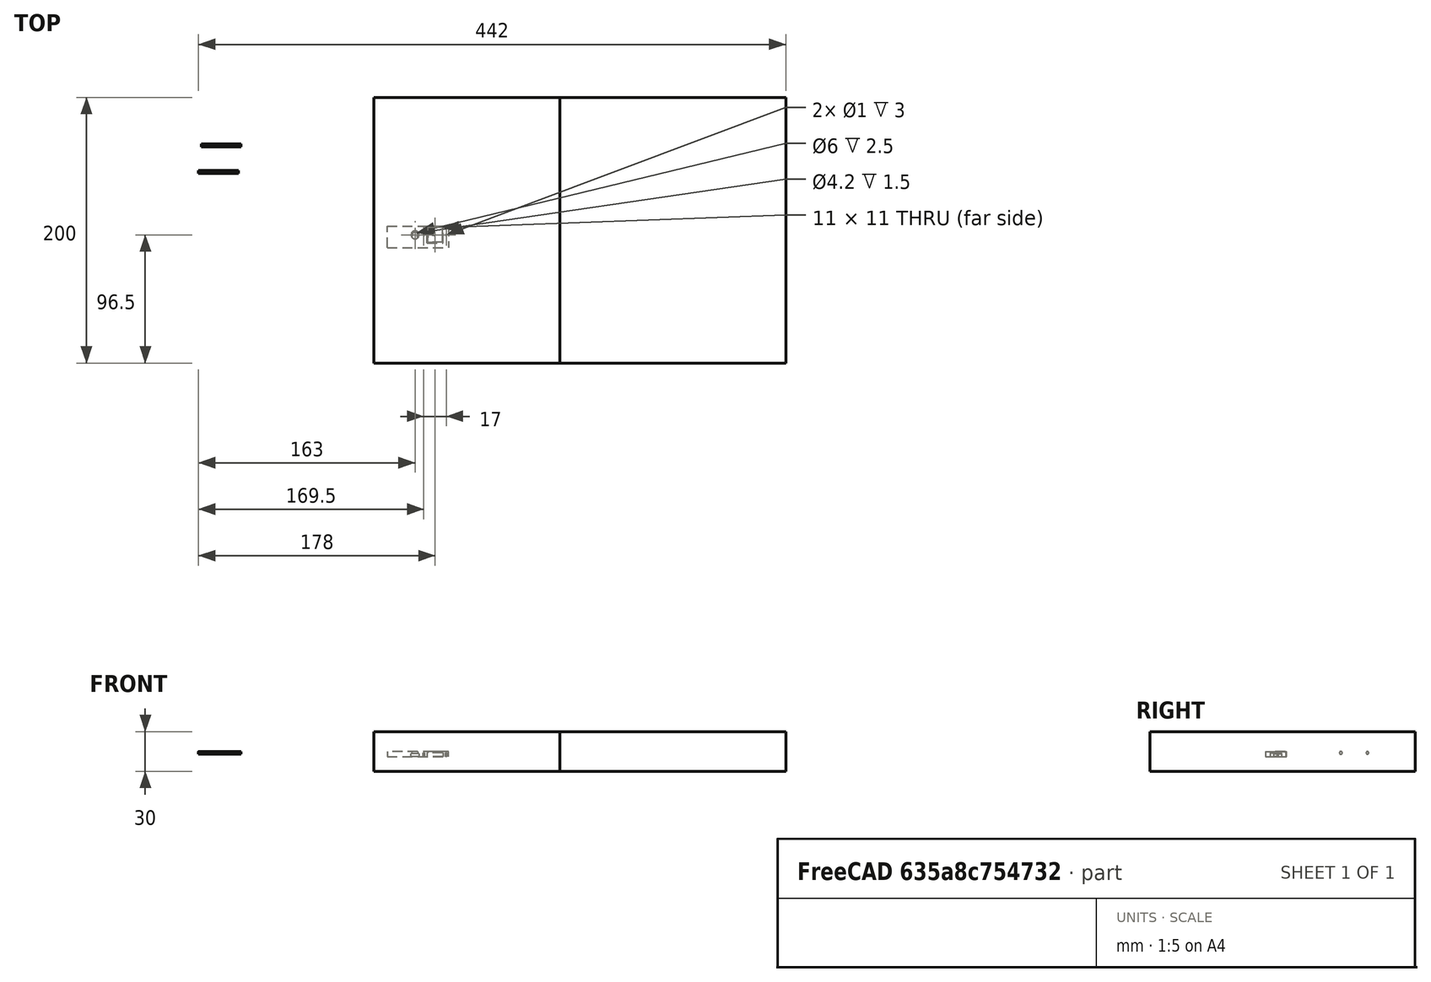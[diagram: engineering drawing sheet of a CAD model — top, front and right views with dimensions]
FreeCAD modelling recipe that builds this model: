
FCSTD DOCUMENT  (FreeCAD 0.17R13522 (Git))
Label: led_2
License: CreativeCommons Attribution-ShareAlike
LicenseURL: http://creativecommons.org/licenses/by-sa/4.0/
objects: Part::Cut×33, Part::Feature×29, Part::Box×10, Part::Fuse×7, Part::Part2DObjectPython×6, Part::Cylinder×4, App::DocumentObjectGroup×3
note: 89 computed .brp shape members not serialized (recipe doc carries the construction recipe); baked Part::Feature solids carry a one-line shape summary decoded from their .brp

FEATURE [Part::Part2DObjectPython] Line009  # Draft 2D object (typed FeaturePython)
  ChamferSize = 0
  Closed = false
  End = (270.847,20.2,0)
  FilletRadius = 0
  Length = 35.3471
  MakeFace = false
  Points = (2) [(235.5,20.2,0),(270.847,20.2,0)]
  Start = (235.5,20.2,0)
  Subdivisions = 0
FEATURE [Part::Part2DObjectPython] Circle001  # Draft 2D object (typed FeaturePython)
  FirstAngle = 0
  LastAngle = 0
  MakeFace = false
  Placement = pos=(259.67,20.2,0) rot=(0,0,1;0rad)
  Radius = 14
FEATURE [Part::Part2DObjectPython] Line014  # Draft 2D object (typed FeaturePython)
  ChamferSize = 0
  Closed = false
  End = (248.272,28.2144,0)
  FilletRadius = 0
  Length = 13.696
  MakeFace = false
  Placement = pos=(-10,0,-4) rot=(0,0,1;0rad)
  Points = (2) [(269.378,20.2,4),(258.272,28.2144,4)]
  Start = (259.378,20.2,0)
  Subdivisions = 0
FEATURE [Part::Part2DObjectPython] Line015  # Draft 2D object (typed FeaturePython)
  ChamferSize = 0
  Closed = false
  End = (254.876,33.263,0)
  FilletRadius = 0
  Length = 13.7518
  MakeFace = false
  Placement = pos=(-10,0,-4) rot=(0,0,1;0rad)
  Points = (2) [(269.174,20.2,4),(264.876,33.263,4)]
  Start = (259.174,20.2,0)
  Subdivisions = 0
FEATURE [Part::Part2DObjectPython] Line016  # Draft 2D object (typed FeaturePython)
  ChamferSize = 0
  Closed = false
  End = (263.227,33.6931,0)
  FilletRadius = 0
  Length = 14.1488
  MakeFace = false
  Placement = pos=(-10,0,-4) rot=(0,0,1;0rad)
  Points = (2) [(268.97,20.2,4),(273.227,33.6931,4)]
  Start = (258.97,20.2,0)
  Subdivisions = 0
FEATURE [Part::Part2DObjectPython] Line017  # Draft 2D object (typed FeaturePython)
  ChamferSize = 0
  Closed = false
  End = (270.612,28.9289,0)
  FilletRadius = 0
  Length = 14.5511
  MakeFace = false
  Placement = pos=(-10,0,-4) rot=(0,0,1;0rad)
  Points = (2) [(268.97,20.2,4),(280.612,28.9289,4)]
  Start = (258.97,20.2,0)
  Subdivisions = 0
FEATURE [App::DocumentObjectGroup] Construction
  Group = -> [Line009,Circle001,Line014,Line015,Line016,Line017]
FEATURE [Part::Box] Box001  label="Cube"
  AttacherType = Attacher::AttachEngine3D
  Height = 3
  Length = 6
  Placement = pos=(39,81,-108) rot=(0,0,1;0rad)
  Width = 6
FEATURE [Part::Feature] Fusion008001001061001  label="panel_siplays_encoders_dobles_y_spacers"
  Placement = pos=(0,0,-105) rot=(0,0,1;0rad)
  shape: bbox 280 x 210 x 10 mm, 411 faces (baked)
FEATURE [Part::Feature] Fusion003002001  label="el perforador001"
  Placement = pos=(48,115,-108) rot=(0,1,0;3.14159rad)
  shape: bbox 22 x 12 x 18 mm, 19 faces (baked)
FEATURE [Part::Feature] Fusion003002001001  label="el perforador002"
  Placement = pos=(87.5,115,-108) rot=(0,1,0;3.14159rad)
  shape: bbox 22 x 12 x 18 mm, 19 faces (baked)
FEATURE [Part::Cut] Cut001001001002003001008002002004
  Base = -> Fusion008001001061001
  Refine = true
  Tool = -> Fusion003002001
FEATURE [Part::Feature] Fusion003002001001001  label="el perforador003"
  Placement = pos=(127,115,-108) rot=(0,1,0;3.14159rad)
  shape: bbox 22 x 12 x 18 mm, 19 faces (baked)
FEATURE [Part::Cut] Cut001001001002003001008002002005
  Base = -> Cut001001001002003001008002002004
  Refine = true
  Tool = -> Fusion003002001001
FEATURE [Part::Feature] Fusion003002001001001001  label="el perforador004"
  Placement = pos=(166.5,115,-108) rot=(0,1,0;3.14159rad)
  shape: bbox 22 x 12 x 18 mm, 19 faces (baked)
FEATURE [Part::Feature] Fusion003002001001001001001  label="el perforador005"
  Placement = pos=(206,115,-108) rot=(0,1,0;3.14159rad)
  shape: bbox 22 x 12 x 18 mm, 19 faces (baked)
FEATURE [Part::Cut] Cut001001001002003001008002002006
  Base = -> Cut001001001002003001008002002005
  Refine = true
  Tool = -> Fusion003002001001001001
FEATURE [Part::Cut] Cut001001001002003001008002002007
  Base = -> Cut001001001002003001008002002006
  Refine = true
  Tool = -> Fusion003002001001001001001
FEATURE [Part::Feature] Fusion003002001001001001002001001  label="el perforador008"
  Placement = pos=(127,40,-108) rot=(0,1,0;3.14159rad)
  shape: bbox 22 x 12 x 18 mm, 19 faces (baked)
FEATURE [Part::Feature] Fusion003002001001001001002001002  label="el perforador009"
  Placement = pos=(127,80.5,-108) rot=(0,1,0;3.14159rad)
  shape: bbox 22 x 12 x 18 mm, 19 faces (baked)
FEATURE [Part::Feature] Fusion003002001001001001002001  label="el perforador007"
  Placement = pos=(127,55,-108) rot=(0,1,0;3.14159rad)
  shape: bbox 22 x 12 x 18 mm, 19 faces (baked)
FEATURE [Part::Feature] Fusion003002001001001001002  label="el perforador006"
  Placement = pos=(127,95.5,-108) rot=(0,1,0;3.14159rad)
  shape: bbox 22 x 12 x 18 mm, 19 faces (baked)
FEATURE [Part::Cut] Cut001001001002003001008002002008
  Base = -> Cut001001001002003001008002002007
  Refine = true
  Tool = -> Fusion003002001001001
FEATURE [Part::Cut] Cut001001001002003001008002002009
  Base = -> Cut001001001002003001008002002008
  Refine = true
  Tool = -> Fusion003002001001001001002
FEATURE [Part::Cut] Cut001001001002003001008002002010
  Base = -> Cut001001001002003001008002002009
  Refine = true
  Tool = -> Fusion003002001001001001002001
FEATURE [Part::Box] Box001001002002002001003001001004001001001001001001002  label="Cube034"
  AttacherType = Attacher::AttachEngine3D
  Height = 4
  Length = 32
  Placement = pos=(200,15,-108) rot=(0,0,1;0rad)
  Width = 10
FEATURE [Part::Fuse] Fusion003002001001001001002001003
  Base = -> Cut001001001002003001008002002010
  Refine = true
  Tool = -> Box001001002002002001003001001004001001001001001001002
FEATURE [Part::Fuse] Fusion003002001001001001002001004
  Base = -> Box001001002002002001003001001004001001001001001001002
  Refine = true
  Tool = -> Fusion003002001001001001002001003
FEATURE [Part::Fuse] Fusion003002001001001001002001005
  Refine = true
  Tool = -> Fusion003002001001001001002001004
FEATURE [Part::Fuse] Fusion003002001001001001002001006
  Base = -> Box001
  Refine = true
  Tool = -> Fusion003002001001001001002001005
FEATURE [Part::Feature] Fusion003002001001001001002001002001  label="el perforador010"
  Placement = pos=(47,80.5,-108) rot=(0,1,0;3.14159rad)
  shape: bbox 22 x 12 x 18 mm, 19 faces (baked)
FEATURE [Part::Feature] Fusion003002001001001001002001002002  label="el perforador011"
  Placement = pos=(87,80.5,-108) rot=(0,1,0;3.14159rad)
  shape: bbox 22 x 12 x 18 mm, 19 faces (baked)
FEATURE [Part::Feature] Fusion003002001001001001002001001001  label="el perforador012"
  Placement = pos=(87,40,-108) rot=(0,1,0;3.14159rad)
  shape: bbox 22 x 12 x 18 mm, 19 faces (baked)
FEATURE [Part::Feature] Fusion003002001001001001002001001001001  label="el perforador013"
  Placement = pos=(47,40,-108) rot=(0,1,0;3.14159rad)
  shape: bbox 22 x 12 x 18 mm, 19 faces (baked)
FEATURE [Part::Cut] Cut001001001002003001008002002011
  Base = -> Fusion003002001001001001002001006
  Refine = true
  Tool = -> Fusion003002001001001001002001002
FEATURE [Part::Cut] Cut001001001002003001008002002012
  Base = -> Cut001001001002003001008002002011
  Refine = true
  Tool = -> Fusion003002001001001001002001002002
FEATURE [Part::Cut] Cut001001001002003001008002002013
  Base = -> Cut001001001002003001008002002012
  Refine = true
  Tool = -> Fusion003002001001001001002001002001
FEATURE [Part::Cut] Cut001001001002003001008002002014
  Base = -> Cut001001001002003001008002002013
  Refine = true
  Tool = -> Fusion003002001001001001002001001001001
FEATURE [Part::Feature] Fusion003002001001001001002001001001002  label="el perforador014"
  Placement = pos=(220,8,-108) rot=(0.707107,0.707107,0;3.14159rad)
  shape: bbox 12 x 22 x 18 mm, 19 faces (baked)
FEATURE [Part::Cut] Cut001001001002003001008002002015
  Base = -> Cut001001001002003001008002002014
  Refine = true
  Tool = -> Fusion003002001001001001002001001001
FEATURE [Part::Cut] Cut001001001002003001008002002016
  Base = -> Cut001001001002003001008002002015
  Refine = true
  Tool = -> Fusion003002001001001001002001001
FEATURE [Part::Cut] Cut001001001002003001008002002017  label="base solo faltan los leds"
  Base = -> Cut001001001002003001008002002016
  Refine = true
  Tool = -> Fusion003002001001001001002001001001002
FEATURE [Part::Feature] Fusion001001  label="perforador led 3 mm001 rojo com2"
  Placement = pos=(24,43,-108) rot=(0,1,0;3.14159rad)
  shape: bbox 6 x 6 x 10 mm, 13 faces (baked)
FEATURE [Part::Feature] Fusion003002001001001001002001001001003  label="perforador led 3 mm002 rojo nav2"
  Placement = pos=(61,43,-108) rot=(0,1,0;3.14159rad)
  shape: bbox 6 x 6 x 10 mm, 13 faces (baked)
FEATURE [Part::Feature] Fusion003002001001001001002001001001004  label="perforador led 3 mm002 rojo adf2"
  Placement = pos=(101,43,-108) rot=(0,1,0;3.14159rad)
  shape: bbox 6 x 6 x 10 mm, 13 faces (baked)
FEATURE [Part::Feature] Fusion003002001001001001002001001001005  label="perforador led 3 mm001 rojo com1"
  Placement = pos=(24,83.5,-108) rot=(0,1,0;3.14159rad)
  shape: bbox 6 x 6 x 10 mm, 13 faces (baked)
FEATURE [Part::Feature] Fusion003002001001001001002001001001006  label="perforador led 3 mm002 rojo nav1"
  Placement = pos=(61,83.5,-108) rot=(0,1,0;3.14159rad)
  shape: bbox 6 x 6 x 10 mm, 13 faces (baked)
FEATURE [Part::Feature] Fusion003002001001001001002001001001007  label="perforador led 3 mm002 rojo adf1"
  Placement = pos=(101,83.5,-108) rot=(0,1,0;3.14159rad)
  shape: bbox 6 x 6 x 10 mm, 13 faces (baked)
FEATURE [Part::Cut] Cut
  Base = -> Cut001001001002003001008002002017
  Refine = true
  Tool = -> Fusion003002001001001001002001001001005
FEATURE [Part::Cut] Cut001001001002003001008002002018
  Base = -> Cut
  Refine = true
  Tool = -> Fusion003002001001001001002001001001006
FEATURE [Part::Cut] Cut001001001002003001008002002019
  Base = -> Cut001001001002003001008002002018
  Refine = true
  Tool = -> Fusion003002001001001001002001001001007
FEATURE [Part::Cut] Cut001001001002003001008002002020
  Base = -> Cut001001001002003001008002002019
  Refine = true
  Tool = -> Fusion003002001001001001002001001001004
FEATURE [Part::Cut] Cut001001001002003001008002002021
  Base = -> Cut001001001002003001008002002020
  Refine = true
  Tool = -> Fusion003002001001001001002001001001003
FEATURE [Part::Cut] Cut001001001002003001008002002022
  Base = -> Cut001001001002003001008002002021
  Refine = true
  Tool = -> Fusion001001
FEATURE [Part::Feature] Fusion003002001001001001002001001001008  label="perforador led 5 mm sound marker"
  Placement = pos=(40.75,133,-108) rot=(0,1,0;3.14159rad)
  shape: bbox 7.5 x 7.5 x 10 mm, 13 faces (baked)
FEATURE [Part::Feature] Fusion003002001001001001002001001001009  label="perforador led 5 mm sound com1"
  Placement = pos=(80.25,133,-108) rot=(0,1,0;3.14159rad)
  shape: bbox 7.5 x 7.5 x 10 mm, 13 faces (baked)
FEATURE [Part::Feature] Fusion003002001001001001002001001001010  label="perforador led 5 mm sound nav1"
  Placement = pos=(119.75,133,-108) rot=(0,1,0;3.14159rad)
  shape: bbox 7.5 x 7.5 x 10 mm, 13 faces (baked)
FEATURE [Part::Feature] Fusion003002001001001001002001001001011  label="perforador led 5 mm sound dme"
  Placement = pos=(159.25,133,-108) rot=(0,1,0;3.14159rad)
  shape: bbox 7.5 x 7.5 x 10 mm, 13 faces (baked)
FEATURE [Part::Feature] Fusion003002001001001001002001001001012  label="perforador led 5 mm sound adf1"
  Placement = pos=(198.75,133,-108) rot=(0,1,0;3.14159rad)
  shape: bbox 7.5 x 7.5 x 10 mm, 13 faces (baked)
FEATURE [Part::Feature] Fusion003002001001001001002001001001013  label="perforador led 5 mm ON/OFF"
  Placement = pos=(263.5,133,-108) rot=(0,1,0;3.14159rad)
  shape: bbox 7.5 x 7.5 x 10 mm, 13 faces (baked)
FEATURE [Part::Cut] Cut001001001002003001008002002023
  Base = -> Cut001001001002003001008002002022
  Refine = true
  Tool = -> Fusion003002001001001001002001001001013
FEATURE [Part::Cut] Cut001001001002003001008002002024
  Base = -> Cut001001001002003001008002002023
  Refine = true
  Tool = -> Fusion003002001001001001002001001001012
FEATURE [Part::Cut] Cut001001001002003001008002002025
  Base = -> Cut001001001002003001008002002024
  Refine = true
  Tool = -> Fusion003002001001001001002001001001011
FEATURE [Part::Cut] Cut001001001002003001008002002026
  Base = -> Cut001001001002003001008002002025
  Refine = true
  Tool = -> Fusion003002001001001001002001001001010
FEATURE [Part::Cut] Cut001001001002003001008002002027
  Base = -> Cut001001001002003001008002002026
  Refine = true
  Tool = -> Fusion003002001001001001002001001001009
FEATURE [Part::Cut] Cut001001001002003001008002002028
  Base = -> Cut001001001002003001008002002027
  Refine = true
  Tool = -> Fusion003002001001001001002001001001008
FEATURE [Part::Box] Box  label="Cube035"
  AttacherType = Attacher::AttachEngine3D
  Height = 10
  Length = 300
  Placement = pos=(-8,153.85,-111) rot=(0,0,1;0rad)
  Width = 120
FEATURE [Part::Cut] Cut001001001002003001008002002029  label="panel sin letras"
  Base = -> Cut001001001002003001008002002028
  Refine = true
  Tool = -> Box
FEATURE [Part::Box] Box001001002002002001003001001004001001001001001001003  label="cortador saca parte izquierda"
  AttacherType = Attacher::AttachEngine3D
  Height = 30
  Length = 140
  Placement = pos=(-10,-10,-119) rot=(0,0,1;0rad)
  Width = 200
FEATURE [Part::Box] Box001001002002002001003001001004001001001001001001004  label="cortador saca parte derecha"
  AttacherType = Attacher::AttachEngine3D
  Height = 30
  Length = 170
  Placement = pos=(130,-10,-119) rot=(0,0,1;0rad)
  Width = 200
FEATURE [Part::Cylinder] Cylinder  label="clavija agujereadora1_1"
  Angle = 360
  AttacherType = Attacher::AttachEngine3D
  Height = 30
  Placement = pos=(115,111.85,-106) rot=(0,1,0;1.5708rad)
  Radius = 1.05
FEATURE [Part::Cylinder] Cylinder001  label="clavija agujereadora2_1"
  Angle = 360
  AttacherType = Attacher::AttachEngine3D
  Height = 30
  Placement = pos=(115,37.85,-106) rot=(0,1,0;1.5708rad)
  Radius = 1.05
FEATURE [Part::Cylinder] Cylinder002  label="clavija empalmadora1"
  Angle = 360
  AttacherType = Attacher::AttachEngine3D
  Height = 29.8
  Placement = pos=(-140,153.85,-105) rot=(0,1,0;1.5708rad)
  Radius = 1
FEATURE [Part::Cut] Cut001001001002003001008002002030
  Base = -> Cut001001001002003001008002002029
  Refine = true
  Tool = -> Cylinder
FEATURE [Part::Cut] Cut001001001002003001008002002031  label="panel sin letras con agujeros clavijas"
  Base = -> Cut001001001002003001008002002030
  Refine = true
  Tool = -> Cylinder001
FEATURE [App::DocumentObjectGroup] Group  label="cortadores principales"
  Group = -> [Box001001002002002001003001001004001001001001001001003,Box001001002002002001003001001004001001001001001001004]
FEATURE [Part::Cylinder] Cylinder003  label="clavija hace agujero"
  Angle = 360
  AttacherType = Attacher::AttachEngine3D
  Height = 30
  Placement = pos=(-142,133.85,-105) rot=(0,1,0;1.5708rad)
  Radius = 1.05
FEATURE [App::DocumentObjectGroup] Group001  label="clavijas"
  Group = -> [Cylinder003,Cylinder002]
FEATURE [Part::Box] Box001001002002002001003001001004001001001001001001006  label="fleje abajo"
  AttacherType = Attacher::AttachEngine3D
  Height = 4
  Length = 280
  Placement = pos=(0,-4,-108) rot=(0,0,1;0rad)
  Width = 4
FEATURE [Part::Fuse] Fusion
  Base = -> Cut001001001002003001008002002031
  Refine = true
  Tool = -> Box001001002002002001003001001004001001001001001001006
FEATURE [Part::Feature] Cylinder002001  label="clavija empalmadora une frente base"
  Placement = pos=(30,-2,-134) rot=(0,0,1;1.5708rad)
  shape: bbox 2 x 2 x 29.8 mm, 3 faces (baked)
FEATURE [Part::Feature] Cylinder002001001  label="clavija empalmadora une frente base2"
  Placement = pos=(250,-2,-134) rot=(0,0,1;1.5708rad)
  shape: bbox 2 x 2 x 29.8 mm, 3 faces (baked)
FEATURE [Part::Fuse] Fusion003002001001001001002001001001014
  Base = -> Fusion
  Refine = true
  Tool = -> Cylinder002001
FEATURE [Part::Fuse] Fusion003002001001001001002001001001015  label="frente con clavijas sin letras"
  Base = -> Cylinder002001001
  Refine = true
  Tool = -> Fusion003002001001001001002001001001014
FEATURE [Part::Box] Box001001002002002001003001001004001001001001001001007  label="cortador clavijas"
  AttacherType = Attacher::AttachEngine3D
  Height = 4
  Length = 280
  Placement = pos=(0,0,-153) rot=(1,0,0;1.5708rad)
  Width = 30
FEATURE [Part::Cut] Cut001001001002003001008002002032  label="frente con clavijas de 15 sin letras"
  Base = -> Fusion003002001001001001002001001001015
  Refine = true
  Tool = -> Box001001002002002001003001001004001001001001001001007
FEATURE [Part::Box] Box001001002002002001003001001004001001001001001001008  label="Cube036"
  AttacherType = Attacher::AttachEngine3D
  Height = 60
  Length = 300
  Placement = pos=(46,-26,-134) rot=(0,0,1;0rad)
  Width = 200
FEATURE [Part::Cut] Cut001001001002003001008002002033
  Base = -> Cut001001001002003001008002002032
  Refine = true
  Tool = -> Box001001002002002001003001001004001001001001001001008
FEATURE [Part::Box] Box001001002002002001003001001004001001001001001001009  label="Cube037"
  AttacherType = Attacher::AttachEngine3D
  Height = 60
  Length = 100
  Placement = pos=(-22,-23,-132) rot=(0,0,1;0rad)
  Width = 100
FEATURE [Part::Cut] Cut001001001002003001008002002034
  Base = -> Cut001001001002003001008002002033
  Refine = true
  Tool = -> Box001001002002002001003001001004001001001001001001009
FEATURE [Part::Box] Box001001002002002001003001001004001001001001001001010  label="Cube038"
  AttacherType = Attacher::AttachEngine3D
  Height = 60
  Length = 100
  Placement = pos=(-10,93,-125) rot=(0,0,1;0rad)
  Width = 100
FEATURE [Part::Cut] Cut001001001002003001008002002035
  Base = -> Cut001001001002003001008002002034
  Refine = true
  Tool = -> Box001001002002002001003001001004001001001001001001010
